# Revit family: Duct_Door-Acudor-Surface_Mount-CD-5080-F_Series
name_source: partatom
category: Specialty Equipment
revit_build: Autodesk Revit 2014 (Build: 20130308_1515(x64)
units: mm (PartAtom-declared; Revit-internal decimal feet)

## types (9) — shared parameters
Assembly Code = C1020700
Ceiling-Mounted = Yes
Description = Beveled Universal Flush
Finish = Galvanized Steel-Acudor-24 Gauge-Satin
Installation Type = Surface Mount
Length = 9/16"
Manufacturer = Acudor
Material = Galvanized Steel-Acudor-24 Gauge-Satin
Product Documentation Link = https://www.acudor.com
Product Page URL = https://www.acudor.com
URL = http://acudor.com
Wall Mounted = No

## per-type parameters (varying)
| type | 2 Latch | 4 Latch | Cylinder Lock | Default Elevation | Height | Latch Offset | Other Latch Offset | Width |
| CD-5080-F 6x6 | Yes | No | No | 0" | 6" | 3" | 2" | 6" |
| CD-5080-F 8x8 | Yes | No | Yes | 48" | 8" | 4" | 2 21/32" | 8" |
| CD-5080-F 10x10 | Yes | No | Yes | 48" | 10" | 5" | 3 11/32" | 10" |
| CD-5080-F 12x12 | Yes | No | Yes | 48" | 12" | 6" | 4" | 12" |
| CD-5080-F 14x14 | No | Yes | Yes | 48" | 14" | 3 1/2" | 3 1/2" | 14" |
| CD-5080-F 16x16 | No | Yes | Yes | 48" | 16" | 4" | 4" | 16" |
| CD-5080-F 18x18 | No | Yes | Yes | 48" | 18" | 4 1/2" | 4 1/2" | 18" |
| CD-5080-F 20x20 | No | Yes | Yes | 48" | 20" | 5" | 5" | 20" |
| CD-5080-F 24x24 | No | Yes | Yes | 48" | 24" | 6" | 6" | 24" |

note: column(s) folded — value = type name in every type: Model

## geometry (parser evidence)
native form markers: Sweep x4
no freeform markers — native parametric forms only
